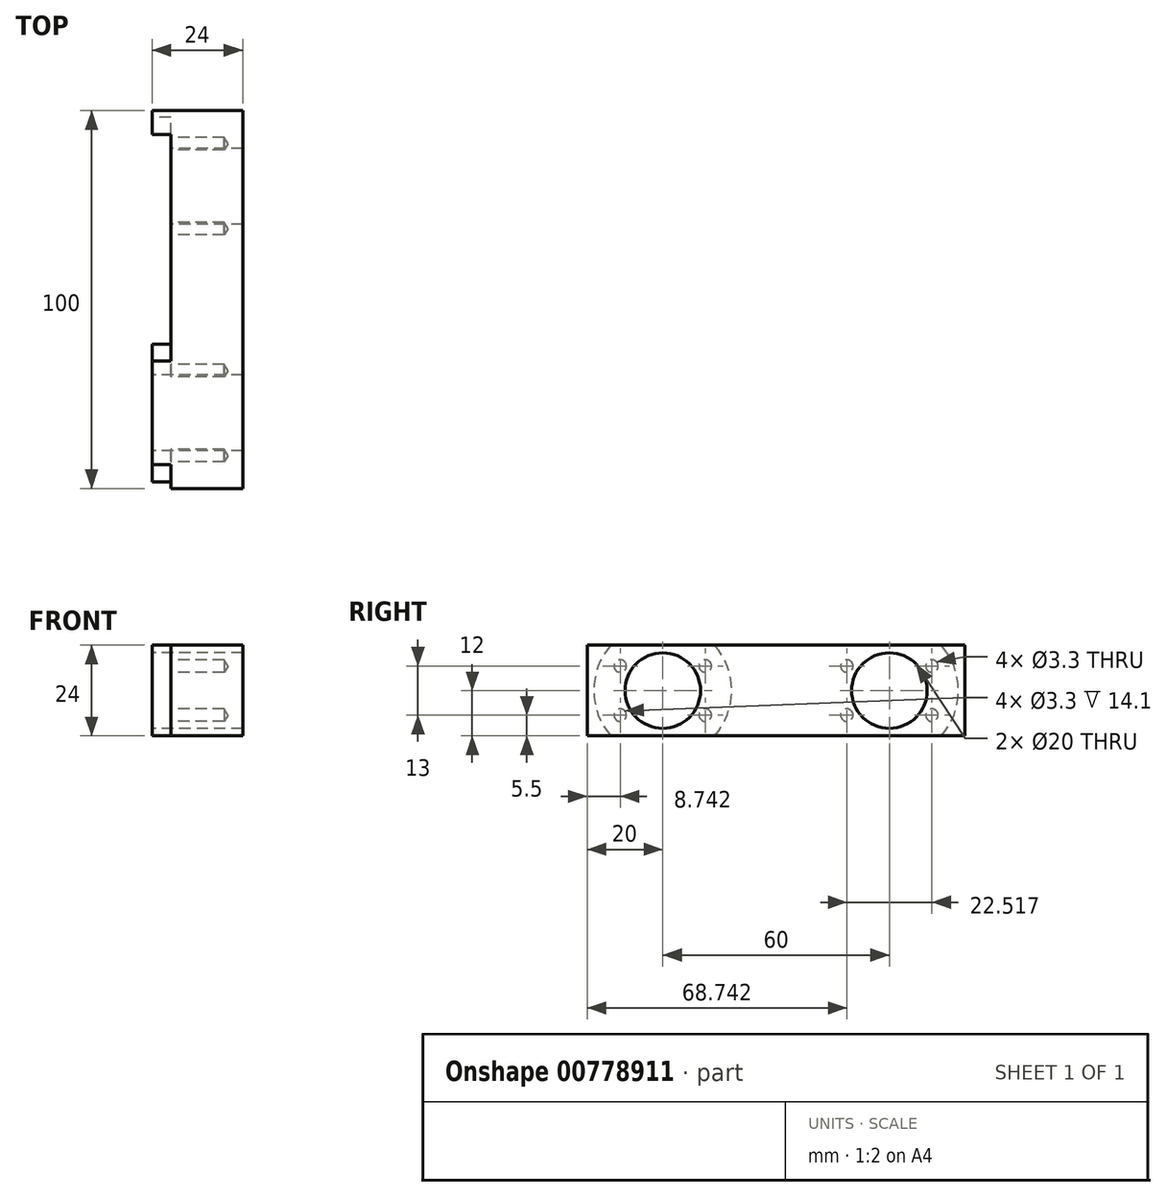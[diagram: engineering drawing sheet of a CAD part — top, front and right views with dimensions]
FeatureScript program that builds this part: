
annotation { "Feature Type Name" : "Feature", "Feature Type Description" : "" }
export const myFeature = defineFeature(function(context is Context, id is Id, definition is map)
    precondition{}
    {
        {
            var Q0;
            Q0=qCreatedBy(makeId("Right.planeOp"),FACE);
            var sketch = newSketch(context, id + "F0", { "sketchPlane" : qUnion([Q0])});
            skLineSegment(sketch, "E0.bottom", {"start": v(50, -12) * mm, "end": v(-50, -12) * mm});
            skLineSegment(sketch, "E0.top", {"start": v(50, 12) * mm, "end": v(-50, 12) * mm});
            skLineSegment(sketch, "E0.left", {"start": v(50, -12) * mm, "end": v(50, 12) * mm});
            skLineSegment(sketch, "E0.right", {"start": v(-50, -12) * mm, "end": v(-50, 12) * mm});
            skPoint(sketch, "E0.middle", {"position": v(0, 0) * mm});
            skPoint(sketch, "E1", {"position": v(-30, 0) * mm});
            skCircle(sketch, "E2", {"center": v(-30, 0) * mm, "radius": 10 * mm});
            skCircle(sketch, "E3.MirrorC", {"center": v(30, 0) * mm, "radius": 10 * mm});
            skSolve(sketch);
        }
        {
            var Q0;
            Q0=makeQuery(id+"F0.imprint","IMPRINT",FACE,{"disambiguationData":[TD([[makeQuery(id+"F0.imprint","IMPRINT",EDGE,{"derivedFrom":sQuery(id+"F0.wireOp",EDGE,"E0.bottom")}),-1.0]])]});
            extrude(context, id + "F1", {"entities" : qUnion([Q0]), "depth" : 24 * mm, "offsetDistance" : 25 * mm});
        }
        {
            var Q0;
            Q0=makeQuery(id+"F1.opExtrude","CAP_FACE",FACE,{"disambiguationData":[OSD([sQuery(id+"F0.wireOp",EDGE,"E0.bottom"),sQuery(id+"F0.wireOp",EDGE,"E0.top"),sQuery(id+"F0.wireOp",EDGE,"E0.left"),sQuery(id+"F0.wireOp",EDGE,"E0.right"),sQuery(id+"F0.wireOp",EDGE,"E2"),sQuery(id+"F0.wireOp",EDGE,"E3.MirrorC")])],"isStart":true});
            var sketch = newSketch(context, id + "F2", { "sketchPlane" : qUnion([Q0])});
            skCircle(sketch, "E4", {"center": v(-30, 0) * mm, "radius": 18.25 * mm});
            skCircle(sketch, "E5.MirrorC", {"center": v(30, 0) * mm, "radius": 18.25 * mm});
            skSolve(sketch);
        }
        {
            var Q0;
            Q0=makeQuery(id+"F2.imprint","IMPRINT",FACE,{"disambiguationData":[TD([[makeQuery(id+"F2.imprint","IMPRINT",EDGE,{"derivedFrom":sQuery(id+"F2.wireOp",EDGE,"E4")}),1.0]])]});
            var Q1;
            Q1=makeQuery(id+"F2.imprint","IMPRINT",FACE,{"disambiguationData":[TD([[makeQuery(id+"F2.imprint","IMPRINT",EDGE,{"derivedFrom":sQuery(id+"F2.wireOp",EDGE,"E5.MirrorC")}),-1.0]])]});
            extrude(context, id + "F3", {"entities" : qUnion([Q0, Q1]), "operationType" : NewBodyOperationType.REMOVE, "oppositeDirection" : true, "depth" : 5 * mm, "offsetDistance" : 25 * mm});
        }
        {
            var Q0;
            Q0=makeQuery(id+"F3.boolean.opBoolean","COPY",FACE,{"derivedFrom":makeQuery(id+"F3.opExtrude","CAP_FACE",FACE,{"disambiguationData":[OSD([sQuery(id+"F0.wireOp",EDGE,"E3.MirrorC"),sQuery(id+"F2.wireOp",EDGE,"E4")])],"isStart":false})});
            var sketch = newSketch(context, id + "F4", { "sketchPlane" : qUnion([Q0])});
            skPoint(sketch, "E6", {"position": v(-43, 0) * mm});
            skPoint(sketch, "E7", {"position": v(-30, 0) * mm});
            skCircle(sketch, "E8", {"center": v(-30, 0) * mm, "radius": 13 * mm, "construction": true});
            skCircle(sketch, "E9.MirrorC", {"center": v(30, 0) * mm, "radius": 13 * mm, "construction": true});
            skPoint(sketch, "E10", {"position": v(-41.26, 6.5) * mm});
            skPoint(sketch, "E11", {"position": v(-18.74, 6.5) * mm});
            skPoint(sketch, "E12.MirrorP", {"position": v(-41.26, -6.5) * mm});
            skPoint(sketch, "E13.MirrorP", {"position": v(-18.74, -6.5) * mm});
            skPoint(sketch, "E14.MirrorP", {"position": v(41.26, 6.5) * mm});
            skPoint(sketch, "E15.MirrorP", {"position": v(41.26, -6.5) * mm});
            skPoint(sketch, "E16.MirrorP", {"position": v(18.74, 6.5) * mm});
            skPoint(sketch, "E17.MirrorP", {"position": v(18.74, -6.5) * mm});
            skSolve(sketch);
        }
        {
            var Q0;
            Q0=sQuery(id+"F4.wireOp",VERTEX,"E10");
            var Q1;
            Q1=sQuery(id+"F4.wireOp",VERTEX,"E12.MirrorP");
            var Q2;
            Q2=sQuery(id+"F4.wireOp",VERTEX,"E11");
            var Q3;
            Q3=sQuery(id+"F4.wireOp",VERTEX,"E13.MirrorP");
            var Q4;
            Q4=sQuery(id+"F4.wireOp",VERTEX,"E16.MirrorP");
            var Q5;
            Q5=sQuery(id+"F4.wireOp",VERTEX,"E17.MirrorP");
            var Q6;
            Q6=sQuery(id+"F4.wireOp",VERTEX,"E14.MirrorP");
            var Q7;
            Q7=sQuery(id+"F4.wireOp",VERTEX,"E15.MirrorP");
            var Q8;
            Q8=makeQuery(id+"F1.opExtrude","SWEPT_BODY",BODY,{"disambiguationData":[OSD([sQuery(id+"F0.wireOp",EDGE,"E0.bottom"),sQuery(id+"F0.wireOp",EDGE,"E0.top"),sQuery(id+"F0.wireOp",EDGE,"E0.left"),sQuery(id+"F0.wireOp",EDGE,"E0.right"),sQuery(id+"F0.wireOp",EDGE,"E2"),sQuery(id+"F0.wireOp",EDGE,"E3.MirrorC")])]});
            hole(context, id + "F5", {"style" : HoleStyle.SIMPLE, "endStyle" : HoleEndStyle.BLIND, "standardTappedOrClearance" : lookupTablePath({ "standard" : "ISO", "engagement" : "75%", "pitch" : "0.7 mm", "size" : "M4", "type" : "Tapped" }), "standardBlindInLast" : lookupTablePath({ "standard" : "ISO", "engagement" : "75%", "pitch" : "0.7 mm", "size" : "M4", "type" : "Tapped" }), "holeDiameter" : 3.3 * mm, "majorDiameter" : 4 * mm, "showTappedDepth" : true, "holeDepth" : 14.1 * mm, "tappedDepth" : 12 * mm, "tapClearance" : 3, "locations" : qUnion([Q0, Q1, Q2, Q3, Q4, Q5, Q6, Q7]), "scope" : qUnion([Q8])});
        }
    });
